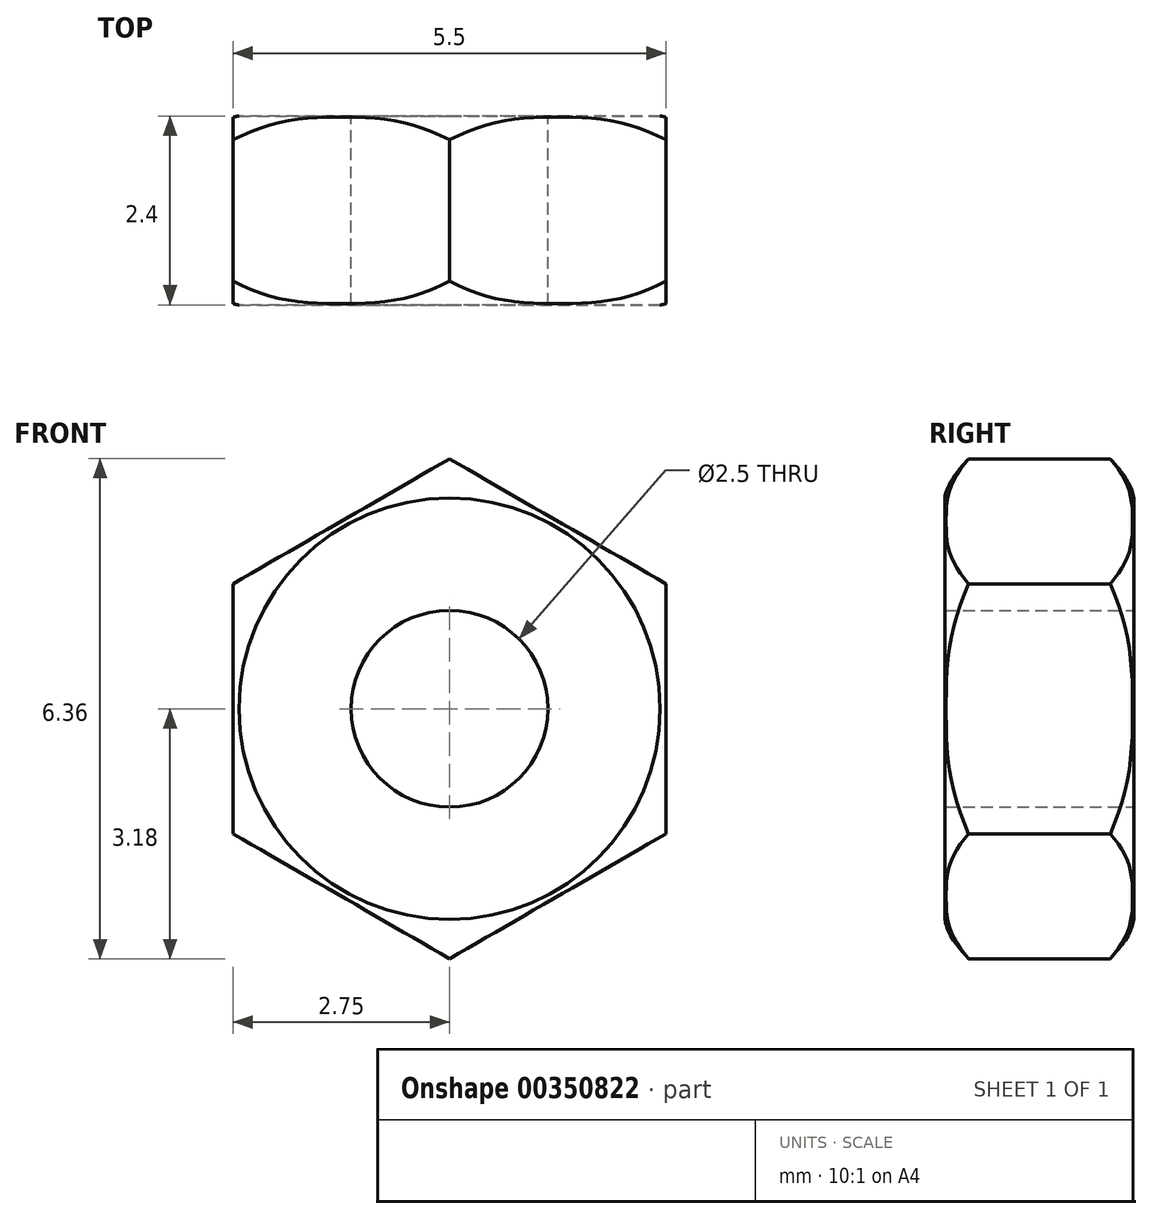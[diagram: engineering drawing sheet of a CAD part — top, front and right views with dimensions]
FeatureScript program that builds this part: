
annotation { "Feature Type Name" : "Feature", "Feature Type Description" : "" }
export const myFeature = defineFeature(function(context is Context, id is Id, definition is map)
    precondition{}
    {
        {
            var Q0;
            Q0=qCreatedBy(makeId("Front.planeOp"),FACE);
            var sketch = newSketch(context, id + "F0", { "sketchPlane" : qUnion([Q0])});
            skCircle(sketch, "E0.cCircle", {"center": v(0, 0) * mm, "radius": 2.75 * mm, "construction": true});
            skLineSegment(sketch, "E0.0", {"start": v(2.75, 1.59) * mm, "end": v(2.75, -1.59) * mm});
            skLineSegment(sketch, "E0.1", {"start": v(2.75, -1.59) * mm, "end": v(0, -3.18) * mm});
            skLineSegment(sketch, "E0.2", {"start": v(0, -3.18) * mm, "end": v(-2.75, -1.59) * mm});
            skLineSegment(sketch, "E0.3", {"start": v(-2.75, -1.59) * mm, "end": v(-2.75, 1.59) * mm});
            skLineSegment(sketch, "E0.4", {"start": v(-2.75, 1.59) * mm, "end": v(0, 3.18) * mm});
            skLineSegment(sketch, "E0.5", {"start": v(0, 3.18) * mm, "end": v(2.75, 1.59) * mm});
            skPoint(sketch, "E0.0.midPoint", {"position": v(2.75, 0) * mm});
            skCircle(sketch, "E1", {"center": v(0, 0) * mm, "radius": 1.25 * mm});
            skSolve(sketch);
        }
        {
            var Q0;
            Q0 = qSketchRegion(id + "F0", true);
            extrude(context, id + "F1", {"entities" : qUnion([Q0]), "depth" : 2.4 * mm});
        }
        {
            var Q0;
            Q0=qCreatedBy(makeId("Right.planeOp"),FACE);
            var sketch = newSketch(context, id + "F2", { "sketchPlane" : qUnion([Q0])});
            skLineSegment(sketch, "E2", {"start": v(0, 0) * mm, "end": v(-2.4, 0) * mm, "construction": true});
            skLineSegment(sketch, "E3.0", {"start": v(-0.3, -3.18) * mm, "end": v(0, -3.18) * mm});
            skLineSegment(sketch, "E4.0", {"start": v(0, -2.68) * mm, "end": v(0, -3.18) * mm});
            skPoint(sketch, "E5.orphan", {"position": v(0, -1.59) * mm});
            skLineSegment(sketch, "E6", {"start": v(-1.2, 0) * mm, "end": v(-1.2, -3.55) * mm, "construction": true});
            skFitSpline(sketch, "E7", {"points": [v(0, -2.68) * mm, v(-0.3, -3.18) * mm], "startDerivative": vector(-0.07, -0.6) * mm, "endDerivative": vector(-0.35, -0.41) * mm});
            skLineSegment(sketch, "E8.MirrorCS", {"start": v(-2.1, -3.18) * mm, "end": v(-2.4, -3.18) * mm});
            skLineSegment(sketch, "E9.MirrorCS", {"start": v(-2.4, -2.68) * mm, "end": v(-2.4, -3.18) * mm});
            skFitSpline(sketch, "E10.MirrorCS", {"points": [v(-2.4, -2.68) * mm, v(-2.1, -3.18) * mm], "startDerivative": vector(0.07, -0.6) * mm, "endDerivative": vector(0.35, -0.41) * mm});
            skSolve(sketch);
        }
        {
            var Q0;
            Q0 = qSketchRegion(id + "F2", true);
            var Q1;
            Q1=sQuery(id+"F2.wireOp",EDGE,"E2");
            revolve(context, id + "F3", {"operationType" : NewBodyOperationType.REMOVE, "entities" : qUnion([Q0]), "axis" : qUnion([Q1]), "revolveType" : RevolveType.FULL});
        }
    });
